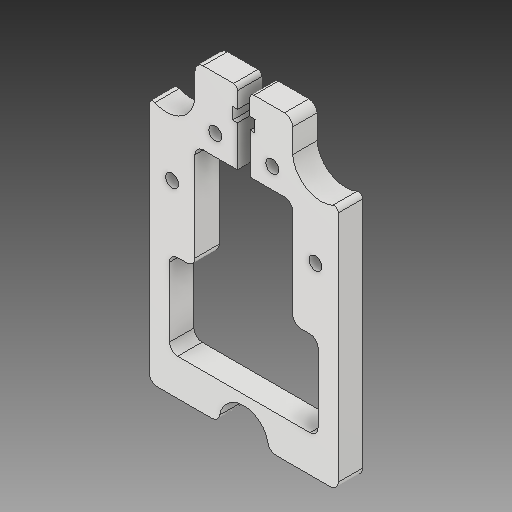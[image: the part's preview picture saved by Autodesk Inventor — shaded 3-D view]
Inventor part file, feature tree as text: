
AUTODESK INVENTOR PART (.ipt)
format: ipt  version: 2018 (Build 220112000, 112)  size: 194,048 bytes
history: native  units: in
note: dims shown in document units (in); Inventor stores cm internally (conversion verified against a paired STEP export)
features: extrude x2, sketch x2, fillet x1
ambient origin geometry x8: Origin, YZ Plane, XZ Plane, XY Plane, X Axis, Y Axis, Z Axis, Center Point
bodies: Solid1 (feature_tree)
feature tree (5):
  extrude  "Extrusion1"  Depth=0.0787in
  extrude  "Extrusion2"  Depth=0.0787in
  fillet  "Fillet1"  Radius=0.2362in
  sketch  "Sketch1"  dims[d0=1.2205in d1=0.2756in d2=0.2756in d6=0.0787in]
  sketch  "Sketch2"  dims[d8=1.1811in d13=0.0787in d14=0.2362in d15=0.0in d16=0.1575in d17=0.2362in d18=0.0in d19=0.0787in]
